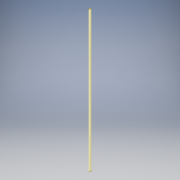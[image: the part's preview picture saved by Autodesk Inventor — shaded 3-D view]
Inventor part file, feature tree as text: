
AUTODESK INVENTOR PART (.ipt)
format: ipt  version: 2019 (Build 230136000, 136)  size: 92,160 bytes
history: native  units: mm
features: revolve x1, sketch x1
ambient origin geometry x8: Origin, YZ Plane, XZ Plane, XY Plane, X Axis, Y Axis, Z Axis, Center Point
bodies: Solid1 (feature_tree)
feature tree (2):
  revolve  "Revolution1"  [1 undecoded]
  sketch  "Sketch1"  dims[d0=2.0mm d1=290.0mm d2=90.0deg]
note: 1 required parameter value undecoded (feature->parameter linkage not recoverable at this tier; creation-order binding heuristic only, values carry confidence <= 0.55)
